# Revit family: НЕВАТОМ_Щит приточно-вытяжной вентиляции  ABU-PW-1-Z, Версия 1
name_source: partatom
category: Электрооборудование
revit_build: Autodesk Revit 2017 (Build: 20170118_1100(x64)
units: mm (PartAtom-declared; Revit-internal decimal feet)

## family parameters
Всегда вертикально = Да
Конфигурация панели = Два столбца, слева направо
На основе рабочей плоскости = Нет
Общий = Нет
При загрузке вырезать с полостями = Нет
Размер круглого соединителя = Использовать диаметр
Тип детали = Щит
Точка расчета площади = Нет

## types (10) — shared parameters
ADSK_Единица измерения = шт.
ADSK_Завод-изготовитель = НЕВАТОМ
ADSK_Количество = 1
ADSK_Напряжение = 380 В

## per-type parameters (varying)
| type | ADSK_Размер_Высота | ADSK_Размер_Длина | ADSK_Размер_Ширина | НЕВАТОМ_Номинальный ток двигателя | НЕВАТОМ_Ориентировочная мощность двигателя | НЕВАТОМ_Преобразователь частоты Danfoss, кВт |
| ABU-РW-1-ZM-0,35/0,35 | 560 мм | 410 мм | 140 мм | 2 А | 0 кВт | ND-051 0,37 кВт для 3 фазы |
| ABU-РW-1-ZM-0,75/0,75 | 560 мм | 410 мм | 140 мм | 3 А | 1 кВт | ND-051 0,75 кВт для 3 фазы |
| ABU-РW-1-ZM-1,5/1,5 | 560 мм | 410 мм | 140 мм | 4 А | 2 кВт | ND-051 1,5 кВт для 3 фазы |
| ABU-РW-1-ZM-2,2/2,2 | 560 мм | 410 мм | 140 мм | 6 А | 2 кВт | ND-051 2,2 кВт для 3 фазы |
| ABU-РW-1-ZM-3,0/3,0 | 560 мм | 410 мм | 140 мм | 10 А | 3 кВт | ND-051 3,0 кВт для 3 фазы |
| ABU-РW-1-ZM-4,0/4,0 | 560 мм | 410 мм | 140 мм | 10 А | 4 кВт | ND-051 4,0 кВт для 3 фазы |
| ABU-РW-1-ZM-5,5/5,5 | 560 мм | 410 мм | 140 мм | 0 А | 0 кВт | ND-051 5,5 кВт для 3 фазы |
| ABU-РW-1-ZM-7,5/7,5 | 560 мм | 410 мм | 140 мм | 18 А | 8 кВт | ND-051 7,5 кВт для 3 фазы |
| ABUm-РW-1-ZM-11/11² | 800 мм | 610 мм | 200 мм | 24 А | 11 кВт | ND-051 11 кВт для 3 фазы |
| ABUm-РW-1-ZM-15/15² | 800 мм | 610 мм | 200 мм | 32 А | 15 кВт | ND-051 15 кВт для 3 фазы |

note: column(s) folded — value = type name in every type: ADSK_Марка, ADSK_Наименование
